# Revit family: Planter_CityScapes
name_source: partatom
category: Generic Models
units: mm (PartAtom-declared; Revit-internal decimal feet)

## family parameters
Always vertical = Yes
Can host rebar = No
Cut with Voids When Loaded = No
Part Type = Normal
Room Calculation Point = No
Round Connector Dimension = Use Diameter
Shared = No
Work Plane-Based = No

## types (6) — shared parameters
CAD Details = https://www.arcat.com
Default Elevation = 0' - 0"
Fascia_Depth = 0' - 0 1/2"
Frame_Thickness = 0' - 2"
Keynote = 32 94 33
Manufacturer = Envisor
Material = <By Category>
PL_Height = 2' - 0"
Product Page URL = https://www.arcat.com
Specification = https://www.arcat.com
TopTrim_Depth = 0' - 0 3/4"
TopTrim_Width = 0' - 4"
URL = https://cityscapesinc.com
VoidDepth = 0' - 0 1/4"

## per-type parameters (varying)
| type | PL_Length | PL_Width |
| 24 x 48 x 24 | 4' - 0" | 2' - 0" |
| 24 x 72 x 24 | 2' - 0" | 6' - 0" |
| 24 x 24 x 24 | 2' - 0" | 2' - 0" |
| 24 x 60 x 24 | 2' - 0" | 5' - 0" |
| 18 x 72 x 24 | 1' - 6" | 6' - 0" |
| 18 x 48 x 24 | 4' - 0" | 1' - 6" |

## geometry (parser evidence)
native form markers: Sweep x2
no freeform markers — native parametric forms only
